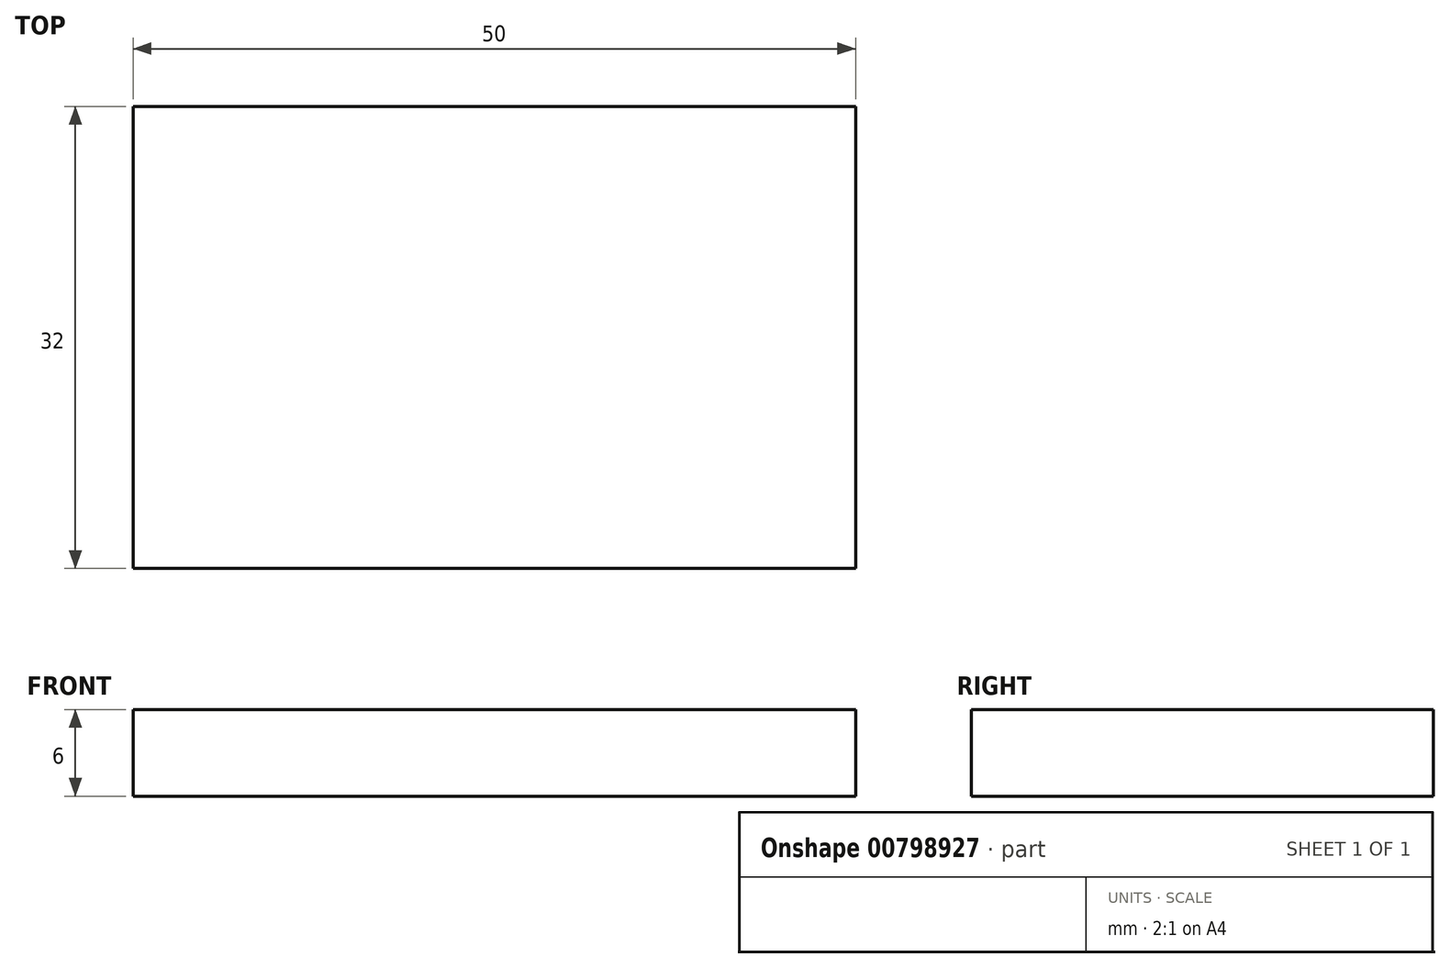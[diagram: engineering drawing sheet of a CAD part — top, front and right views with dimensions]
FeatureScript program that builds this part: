
annotation { "Feature Type Name" : "Feature", "Feature Type Description" : "" }
export const myFeature = defineFeature(function(context is Context, id is Id, definition is map)
    precondition{}
    {
        {
            var Q0;
            Q0=qCreatedBy(makeId("Front.planeOp"),FACE);
            var sketch = newSketch(context, id + "F0", { "sketchPlane" : qUnion([Q0])});
            skLineSegment(sketch, "E0", {"start": v(0, 0) * mm, "end": v(50, 0) * mm});
            skLineSegment(sketch, "E1", {"start": v(50, 0) * mm, "end": v(50, 6) * mm});
            skLineSegment(sketch, "E2", {"start": v(50, 6) * mm, "end": v(0, 6) * mm});
            skLineSegment(sketch, "E3", {"start": v(0, 6) * mm, "end": v(0, 0) * mm});
            skSolve(sketch);
        }
        {
            var Q0;
            Q0=makeQuery(id+"F0.imprint","IMPRINT",FACE,{"disambiguationData":[TD([[makeQuery(id+"F0.imprint","IMPRINT",EDGE,{"derivedFrom":sQuery(id+"F0.wireOp",EDGE,"E0")}),1.0]])]});
            extrude(context, id + "F1", {"entities" : qUnion([Q0]), "depth" : 32 * mm});
        }
    });
